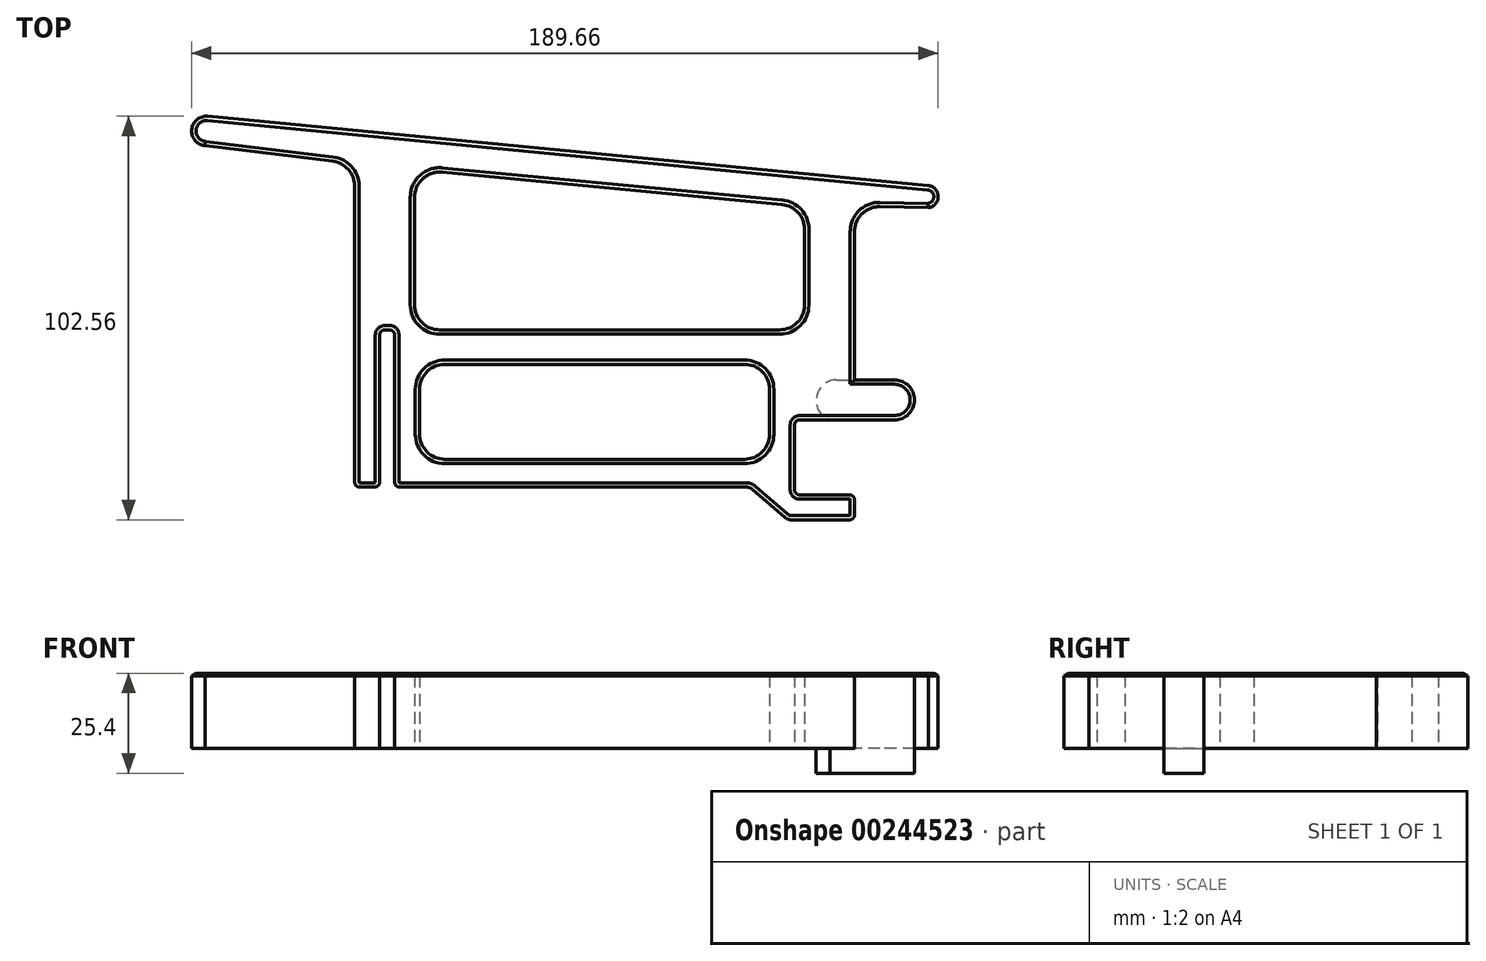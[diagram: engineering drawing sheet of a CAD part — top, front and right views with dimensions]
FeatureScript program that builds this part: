
annotation { "Feature Type Name" : "Feature", "Feature Type Description" : "" }
export const myFeature = defineFeature(function(context is Context, id is Id, definition is map)
    precondition{}
    {
        {
            var Q0;
            Q0=qCreatedBy(makeId("Top.planeOp"),FACE);
            var sketch = newSketch(context, id + "F0", { "sketchPlane" : qUnion([Q0])});
            skLineSegment(sketch, "E0", {"start": v(-47.74, -39.94) * mm, "end": v(26.7, -39.94) * mm});
            skLineSegment(sketch, "E1", {"start": v(38.22, -48.26) * mm, "end": v(52.98, -48.26) * mm});
            skLineSegment(sketch, "E2", {"start": v(54.25, -47) * mm, "end": v(54.25, -43.18) * mm});
            skLineSegment(sketch, "E3", {"start": v(52.98, -41.9) * mm, "end": v(40.28, -41.9) * mm});
            skLineSegment(sketch, "E4", {"start": v(39, -40.64) * mm, "end": v(39, -24.13) * mm});
            skLineSegment(sketch, "E5", {"start": v(40.28, -22.86) * mm, "end": v(56.8, -22.86) * mm});
            skLineSegment(sketch, "E6", {"start": v(54.25, -12.7) * mm, "end": v(54.25, 0) * mm});
            skLineSegment(sketch, "E7", {"start": v(54.25, 0) * mm, "end": v(54.25, 0) * mm});
            skLineSegment(sketch, "E8", {"start": v(54.25, 0) * mm, "end": v(54.25, 24.97) * mm});
            skLineSegment(sketch, "E9", {"start": v(41.55, 25.54) * mm, "end": v(41.55, 6.35) * mm});
            skLineSegment(sketch, "E10", {"start": v(35.2, 0) * mm, "end": v(-51.16, 0) * mm});
            skLineSegment(sketch, "E11", {"start": v(-72.75, 0) * mm, "end": v(-72.75, -24.13) * mm});
            skLineSegment(sketch, "E12", {"start": v(-66.4, -24.13) * mm, "end": v(-66.4, -1.27) * mm});
            skLineSegment(sketch, "E13", {"start": v(-72.75, 0) * mm, "end": v(-72.75, 36.56) * mm});
            skLineSegment(sketch, "E14", {"start": v(-57.51, 33.75) * mm, "end": v(-57.51, 6.35) * mm});
            skLineSegment(sketch, "E15", {"start": v(-50.56, 40.07) * mm, "end": v(35.8, 31.86) * mm});
            skLineSegment(sketch, "E16", {"start": v(-78.33, 42.86) * mm, "end": v(-110.77, 46.8) * mm});
            skLineSegment(sketch, "E17", {"start": v(-110.05, 54.28) * mm, "end": v(72.94, 36.68) * mm});
            skLineSegment(sketch, "E18", {"start": v(72.98, 31.06) * mm, "end": v(60.73, 31.32) * mm});
            skArc(sketch, "E19", {"start": v(-110.05, 54.28) * mm, "mid": v(-114.15, 50.9) * mm, "end": v(-110.77, 46.8) * mm});
            skArc(sketch, "E20", {"start": v(72.98, 31.06) * mm, "mid": v(75.5, 33.9) * mm, "end": v(72.94, 36.68) * mm});
            skLineSegment(sketch, "E21.bottom", {"start": v(-49.9, -8.74) * mm, "end": v(26.3, -8.74) * mm});
            skLineSegment(sketch, "E21.top", {"start": v(-49.9, -32.86) * mm, "end": v(26.3, -32.86) * mm});
            skLineSegment(sketch, "E21.left", {"start": v(-56.24, -15.09) * mm, "end": v(-56.24, -26.51) * mm});
            skLineSegment(sketch, "E21.right", {"start": v(32.66, -15.09) * mm, "end": v(32.66, -26.51) * mm});
            skPoint(sketch, "E22.visualSharp", {"position": v(-57.51, 40.73) * mm});
            skArc(sketch, "E22.filletArc", {"start": v(-50.56, 40.07) * mm, "mid": v(-55.43, 38.45) * mm, "end": v(-57.51, 33.75) * mm});
            skPoint(sketch, "E23.visualSharp", {"position": v(41.55, 31.32) * mm});
            skArc(sketch, "E23.filletArc", {"start": v(41.55, 25.54) * mm, "mid": v(39.9, 29.81) * mm, "end": v(35.8, 31.86) * mm});
            skPoint(sketch, "E24.visualSharp", {"position": v(41.55, 0) * mm});
            skArc(sketch, "E24.filletArc", {"start": v(35.2, 0) * mm, "mid": v(39.69, 1.86) * mm, "end": v(41.55, 6.35) * mm});
            skPoint(sketch, "E25.visualSharp", {"position": v(-57.51, 0) * mm});
            skArc(sketch, "E25.filletArc", {"start": v(-57.51, 6.35) * mm, "mid": v(-55.65, 1.86) * mm, "end": v(-51.16, 0) * mm});
            skPoint(sketch, "E26.visualSharp", {"position": v(-56.24, -8.74) * mm});
            skArc(sketch, "E26.filletArc", {"start": v(-49.9, -8.74) * mm, "mid": v(-54.38, -10.6) * mm, "end": v(-56.24, -15.09) * mm});
            skPoint(sketch, "E27.visualSharp", {"position": v(32.66, -8.74) * mm});
            skArc(sketch, "E27.filletArc", {"start": v(32.66, -15.09) * mm, "mid": v(30.8, -10.6) * mm, "end": v(26.3, -8.74) * mm});
            skPoint(sketch, "E28.visualSharp", {"position": v(32.66, -32.86) * mm});
            skArc(sketch, "E28.filletArc", {"start": v(26.3, -32.86) * mm, "mid": v(30.8, -31) * mm, "end": v(32.66, -26.51) * mm});
            skPoint(sketch, "E29.visualSharp", {"position": v(-56.24, -32.86) * mm});
            skArc(sketch, "E29.filletArc", {"start": v(-56.24, -26.51) * mm, "mid": v(-54.38, -31) * mm, "end": v(-49.9, -32.86) * mm});
            skPoint(sketch, "E30.visualSharp", {"position": v(-54.09, -39.94) * mm});
            skPoint(sketch, "E31.visualSharp", {"position": v(-72.75, 42.18) * mm});
            skArc(sketch, "E31.filletArc", {"start": v(-72.75, 36.56) * mm, "mid": v(-74.35, 40.77) * mm, "end": v(-78.33, 42.86) * mm});
            skPoint(sketch, "E32.visualSharp", {"position": v(54.25, 31.45) * mm});
            skArc(sketch, "E32.filletArc", {"start": v(60.73, 31.32) * mm, "mid": v(56.16, 29.5) * mm, "end": v(54.25, 24.97) * mm});
            skPoint(sketch, "E33.visualSharp", {"position": v(-66.4, -25.4) * mm});
            skPoint(sketch, "E34.visualSharp", {"position": v(-72.75, -25.4) * mm});
            skPoint(sketch, "E35.visualSharp", {"position": v(-66.4, 0) * mm});
            skArc(sketch, "E35.filletArc", {"start": v(-65.13, 0) * mm, "mid": v(-66.03, -0.37) * mm, "end": v(-66.4, -1.27) * mm});
            skPoint(sketch, "E36.visualSharp", {"position": v(-62.6, 0) * mm});
            skPoint(sketch, "E37.visualSharp", {"position": v(-56.24, -25.4) * mm});
            skPoint(sketch, "E38.visualSharp", {"position": v(34.81, -39.94) * mm});
            skPoint(sketch, "E39.visualSharp", {"position": v(36.47, -48.26) * mm});
            skPoint(sketch, "E40.visualSharp", {"position": v(54.25, -48.26) * mm});
            skArc(sketch, "E40.filletArc", {"start": v(52.98, -48.26) * mm, "mid": v(53.88, -47.89) * mm, "end": v(54.25, -47) * mm});
            skPoint(sketch, "E41.visualSharp", {"position": v(54.25, -41.9) * mm});
            skArc(sketch, "E41.filletArc", {"start": v(54.25, -43.18) * mm, "mid": v(53.88, -42.28) * mm, "end": v(52.98, -41.9) * mm});
            skPoint(sketch, "E42.visualSharp", {"position": v(39, -41.9) * mm});
            skArc(sketch, "E42.filletArc", {"start": v(39, -40.64) * mm, "mid": v(39.38, -41.54) * mm, "end": v(40.28, -41.91) * mm});
            skPoint(sketch, "E43.visualSharp", {"position": v(39, -22.86) * mm});
            skArc(sketch, "E43.filletArc", {"start": v(40.28, -22.86) * mm, "mid": v(39.38, -23.23) * mm, "end": v(39, -24.13) * mm});
            skPoint(sketch, "E44.visualSharp", {"position": v(54.25, -22.86) * mm});
            skLineSegment(sketch, "E45", {"start": v(-62.6, -24.13) * mm, "end": v(-62.6, -38.67) * mm});
            skLineSegment(sketch, "E46", {"start": v(-47.74, -39.94) * mm, "end": v(-61.32, -39.94) * mm});
            skLineSegment(sketch, "E47", {"start": v(-72.75, -24.13) * mm, "end": v(-72.75, -38.67) * mm});
            skLineSegment(sketch, "E48", {"start": v(-66.4, -24.13) * mm, "end": v(-66.4, -38.67) * mm});
            skLineSegment(sketch, "E49.trimOffspring", {"start": v(-67.67, -39.94) * mm, "end": v(-71.48, -39.94) * mm});
            skPoint(sketch, "E50.visualSharp", {"position": v(-72.75, -39.94) * mm});
            skArc(sketch, "E50.filletArc", {"start": v(-72.75, -38.67) * mm, "mid": v(-72.38, -39.56) * mm, "end": v(-71.48, -39.94) * mm});
            skPoint(sketch, "E51.visualSharp", {"position": v(-66.4, -39.94) * mm});
            skArc(sketch, "E51.filletArc", {"start": v(-67.67, -39.94) * mm, "mid": v(-66.77, -39.56) * mm, "end": v(-66.4, -38.67) * mm});
            skPoint(sketch, "E52.visualSharp", {"position": v(-62.6, -39.94) * mm});
            skArc(sketch, "E52.filletArc", {"start": v(-62.6, -38.67) * mm, "mid": v(-62.22, -39.56) * mm, "end": v(-61.32, -39.94) * mm});
            skLineSegment(sketch, "E53", {"start": v(36.55, -47.64) * mm, "end": v(28.36, -40.55) * mm});
            skPoint(sketch, "E54.visualSharp", {"position": v(27.64, -39.94) * mm});
            skArc(sketch, "E54.filletArc", {"start": v(28.36, -40.55) * mm, "mid": v(27.58, -40.1) * mm, "end": v(26.7, -39.94) * mm});
            skPoint(sketch, "E55.visualSharp", {"position": v(37.27, -48.26) * mm});
            skArc(sketch, "E55.filletArc", {"start": v(36.55, -47.64) * mm, "mid": v(37.33, -48.1) * mm, "end": v(38.22, -48.26) * mm});
            skLineSegment(sketch, "E56", {"start": v(-60.68, 0) * mm, "end": v(-60.68, 49.53) * mm, "construction": true});
            skLineSegment(sketch, "E57", {"start": v(56.8, -22.86) * mm, "end": v(64.4, -22.86) * mm});
            skLineSegment(sketch, "E58", {"start": v(64.4, -12.7) * mm, "end": v(54.25, -12.7) * mm});
            skArc(sketch, "E59", {"start": v(64.4, -22.86) * mm, "mid": v(69.49, -17.78) * mm, "end": v(64.4, -12.7) * mm});
            skLineSegment(sketch, "E60", {"start": v(-62.6, -24.13) * mm, "end": v(-62.6, -1.27) * mm});
            skLineSegment(sketch, "E61", {"start": v(-65.13, 0) * mm, "end": v(-63.86, 0) * mm});
            skArc(sketch, "E62.filletArc", {"start": v(-62.6, -1.27) * mm, "mid": v(-62.96, -0.37) * mm, "end": v(-63.86, 0) * mm});
            skSolve(sketch);
        }
        {
            var Q0;
            Q0 = qSketchRegion(id + "F0", true);
            extrude(context, id + "F1", {"entities" : qUnion([Q0]), "depth" : 19.05 * mm});
        }
        {
            var Q0;
            Q0=makeQuery(id+"F1.opExtrude","CAP_FACE",FACE,{"disambiguationData":[OSD([sQuery(id+"F0.wireOp",EDGE,"WzjgW17k-lggf-UnH0-HMgM-pe6naiI595cO"),sQuery(id+"F0.wireOp",EDGE,"9XZd8n2k-COVL-yRkC-SFTw-dNNrleFXtEeW"),sQuery(id+"F0.wireOp",EDGE,"ebKL9mH2-Bnui-CzTB-9okA-6eJcoKVjpQ39"),sQuery(id+"F0.wireOp",EDGE,"yKFpFJHV-HY2q-Zi7Z-OOTs-BVQiY6YNlugB"),sQuery(id+"F0.wireOp",EDGE,"E0"),sQuery(id+"F0.wireOp",EDGE,"eVUA3HSm-UM2r-COdl-z2LW-4fUJ3HBTAJpA"),sQuery(id+"F0.wireOp",EDGE,"E1"),sQuery(id+"F0.wireOp",EDGE,"E2"),sQuery(id+"F0.wireOp",EDGE,"E3"),sQuery(id+"F0.wireOp",EDGE,"E4"),sQuery(id+"F0.wireOp",EDGE,"E5"),sQuery(id+"F0.wireOp",EDGE,"E6"),sQuery(id+"F0.wireOp",EDGE,"E8"),sQuery(id+"F0.wireOp",EDGE,"E9"),sQuery(id+"F0.wireOp",EDGE,"E10"),sQuery(id+"F0.wireOp",EDGE,"E11"),sQuery(id+"F0.wireOp",EDGE,"Vu7kB3r5-hH1I-aZOb-dr2h-MKZL5atRk9Tw"),sQuery(id+"F0.wireOp",EDGE,"E12"),sQuery(id+"F0.wireOp",EDGE,"E13"),sQuery(id+"F0.wireOp",EDGE,"E14"),sQuery(id+"F0.wireOp",EDGE,"E15"),sQuery(id+"F0.wireOp",EDGE,"E16"),sQuery(id+"F0.wireOp",EDGE,"E17"),sQuery(id+"F0.wireOp",EDGE,"E18"),sQuery(id+"F0.wireOp",EDGE,"E19"),sQuery(id+"F0.wireOp",EDGE,"E20"),sQuery(id+"F0.wireOp",EDGE,"E21.bottom"),sQuery(id+"F0.wireOp",EDGE,"E21.top"),sQuery(id+"F0.wireOp",EDGE,"E21.left"),sQuery(id+"F0.wireOp",EDGE,"E21.right"),sQuery(id+"F0.wireOp",EDGE,"E22.filletArc"),sQuery(id+"F0.wireOp",EDGE,"E23.filletArc"),sQuery(id+"F0.wireOp",EDGE,"E24.filletArc"),sQuery(id+"F0.wireOp",EDGE,"E25.filletArc"),sQuery(id+"F0.wireOp",EDGE,"E26.filletArc"),sQuery(id+"F0.wireOp",EDGE,"E27.filletArc"),sQuery(id+"F0.wireOp",EDGE,"E28.filletArc"),sQuery(id+"F0.wireOp",EDGE,"E29.filletArc"),sQuery(id+"F0.wireOp",EDGE,"E30.filletArc"),sQuery(id+"F0.wireOp",EDGE,"E31.filletArc"),sQuery(id+"F0.wireOp",EDGE,"E32.filletArc"),sQuery(id+"F0.wireOp",EDGE,"E33.filletArc"),sQuery(id+"F0.wireOp",EDGE,"E34.filletArc"),sQuery(id+"F0.wireOp",EDGE,"4b7fa400-894b-468a-9e9b-99b7c3fb3cf8.filletArc"),sQuery(id+"F0.wireOp",EDGE,"E35.filletArc"),sQuery(id+"F0.wireOp",EDGE,"E36.filletArc"),sQuery(id+"F0.wireOp",EDGE,"E37.filletArc"),sQuery(id+"F0.wireOp",EDGE,"E38.filletArc"),sQuery(id+"F0.wireOp",EDGE,"E39.filletArc"),sQuery(id+"F0.wireOp",EDGE,"E40.filletArc"),sQuery(id+"F0.wireOp",EDGE,"E41.filletArc"),sQuery(id+"F0.wireOp",EDGE,"E42.filletArc"),sQuery(id+"F0.wireOp",EDGE,"E43.filletArc"),sQuery(id+"F0.wireOp",EDGE,"E44.filletArc")])],"isStart":false});
            chamfer(context, id + "F2", {"entities" : qUnion([Q0]), "chamferType" : ChamferType.OFFSET_ANGLE, "width" : 0.64 * mm, "oppositeDirection" : false, "angle" : 60 * degree, "tangentPropagation" : true});
        }
        {
            var Q0;
            Q0=makeQuery(id+"F1.opExtrude","CAP_FACE",FACE,{"disambiguationData":[OSD([sQuery(id+"F0.wireOp",EDGE,"WzjgW17k-lggf-UnH0-HMgM-pe6naiI595cO"),sQuery(id+"F0.wireOp",EDGE,"9XZd8n2k-COVL-yRkC-SFTw-dNNrleFXtEeW"),sQuery(id+"F0.wireOp",EDGE,"E0"),sQuery(id+"F0.wireOp",EDGE,"E1"),sQuery(id+"F0.wireOp",EDGE,"E2"),sQuery(id+"F0.wireOp",EDGE,"E3"),sQuery(id+"F0.wireOp",EDGE,"E4"),sQuery(id+"F0.wireOp",EDGE,"E5"),sQuery(id+"F0.wireOp",EDGE,"E6"),sQuery(id+"F0.wireOp",EDGE,"E8"),sQuery(id+"F0.wireOp",EDGE,"E9"),sQuery(id+"F0.wireOp",EDGE,"E10"),sQuery(id+"F0.wireOp",EDGE,"E11"),sQuery(id+"F0.wireOp",EDGE,"E12"),sQuery(id+"F0.wireOp",EDGE,"E13"),sQuery(id+"F0.wireOp",EDGE,"E14"),sQuery(id+"F0.wireOp",EDGE,"E15"),sQuery(id+"F0.wireOp",EDGE,"E16"),sQuery(id+"F0.wireOp",EDGE,"E17"),sQuery(id+"F0.wireOp",EDGE,"E18"),sQuery(id+"F0.wireOp",EDGE,"E19"),sQuery(id+"F0.wireOp",EDGE,"E20"),sQuery(id+"F0.wireOp",EDGE,"E21.bottom"),sQuery(id+"F0.wireOp",EDGE,"E21.top"),sQuery(id+"F0.wireOp",EDGE,"E21.left"),sQuery(id+"F0.wireOp",EDGE,"E21.right"),sQuery(id+"F0.wireOp",EDGE,"E22.filletArc"),sQuery(id+"F0.wireOp",EDGE,"E23.filletArc"),sQuery(id+"F0.wireOp",EDGE,"E24.filletArc"),sQuery(id+"F0.wireOp",EDGE,"E25.filletArc"),sQuery(id+"F0.wireOp",EDGE,"E26.filletArc"),sQuery(id+"F0.wireOp",EDGE,"E27.filletArc"),sQuery(id+"F0.wireOp",EDGE,"E28.filletArc"),sQuery(id+"F0.wireOp",EDGE,"E29.filletArc"),sQuery(id+"F0.wireOp",EDGE,"E31.filletArc"),sQuery(id+"F0.wireOp",EDGE,"E32.filletArc"),sQuery(id+"F0.wireOp",EDGE,"E35.filletArc"),sQuery(id+"F0.wireOp",EDGE,"E36.filletArc"),sQuery(id+"F0.wireOp",EDGE,"E40.filletArc"),sQuery(id+"F0.wireOp",EDGE,"E41.filletArc"),sQuery(id+"F0.wireOp",EDGE,"E42.filletArc"),sQuery(id+"F0.wireOp",EDGE,"E43.filletArc"),sQuery(id+"F0.wireOp",EDGE,"E45"),sQuery(id+"F0.wireOp",EDGE,"E46"),sQuery(id+"F0.wireOp",EDGE,"E47"),sQuery(id+"F0.wireOp",EDGE,"E48"),sQuery(id+"F0.wireOp",EDGE,"E49.trimOffspring"),sQuery(id+"F0.wireOp",EDGE,"E50.filletArc"),sQuery(id+"F0.wireOp",EDGE,"E51.filletArc"),sQuery(id+"F0.wireOp",EDGE,"E52.filletArc"),sQuery(id+"F0.wireOp",EDGE,"E53"),sQuery(id+"F0.wireOp",EDGE,"E54.filletArc"),sQuery(id+"F0.wireOp",EDGE,"E55.filletArc"),sQuery(id+"F0.wireOp",EDGE,"E57"),sQuery(id+"F0.wireOp",EDGE,"E58"),sQuery(id+"F0.wireOp",EDGE,"E59")])],"isStart":true});
            var sketch = newSketch(context, id + "F3", { "sketchPlane" : qUnion([Q0])});
            skLineSegment(sketch, "E63.bottom", {"start": v(48.01, 22.86) * mm, "end": v(64.4, 22.86) * mm});
            skLineSegment(sketch, "E63.top", {"start": v(49.7, 12.7) * mm, "end": v(64.4, 12.7) * mm});
            skArc(sketch, "E64", {"start": v(64.4, 12.7) * mm, "mid": v(69.49, 17.78) * mm, "end": v(64.4, 22.86) * mm});
            skArc(sketch, "E65", {"start": v(48.01, 22.86) * mm, "mid": v(44.55, 17.06) * mm, "end": v(49.7, 12.7) * mm});
            skSolve(sketch);
        }
        {
            var Q0;
            Q0 = qSketchRegion(id + "F3", true);
            extrude(context, id + "F4", {"entities" : qUnion([Q0]), "operationType" : NewBodyOperationType.ADD, "depth" : 6.35 * mm});
        }
    });
